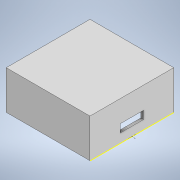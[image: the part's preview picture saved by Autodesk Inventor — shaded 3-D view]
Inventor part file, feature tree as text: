
AUTODESK INVENTOR PART (.ipt)
format: ipt  version: 2022 (Build 260153000, 153)  size: 121,344 bytes
history: native  units: in
note: dims shown in document units (in); Inventor stores cm internally (conversion verified against a paired STEP export)
features: sketch x4, extrude x3
ambient origin geometry x8: Origin, YZ Plane, XZ Plane, XY Plane, X Axis, Y Axis, Z Axis, Center Point
bodies: Solid1 (feature_tree)
feature tree (7):
  extrude  "Extrusion1"  Depth=0.2165in
  extrude  "Extrusion2"  Depth=0.2559in
  sketch  "Sketch5"  dims[d8=0.0787in d9=0.0in d10=0.2559in]
  extrude  "Extrusion3"  Depth=0.2559in
  sketch  "Sketch2"  dims[d2=0.2165in d3=0.2165in]
  sketch  "Sketch4"  dims[d6=0.2559in d7=0.2559in]
  sketch  "Sketch6"  dims[d11=0.0394in d12=0.0in d13=0.0945in d14=0.0472in d15=0.0394in d16=0.0197in d17=-0.2061in]
